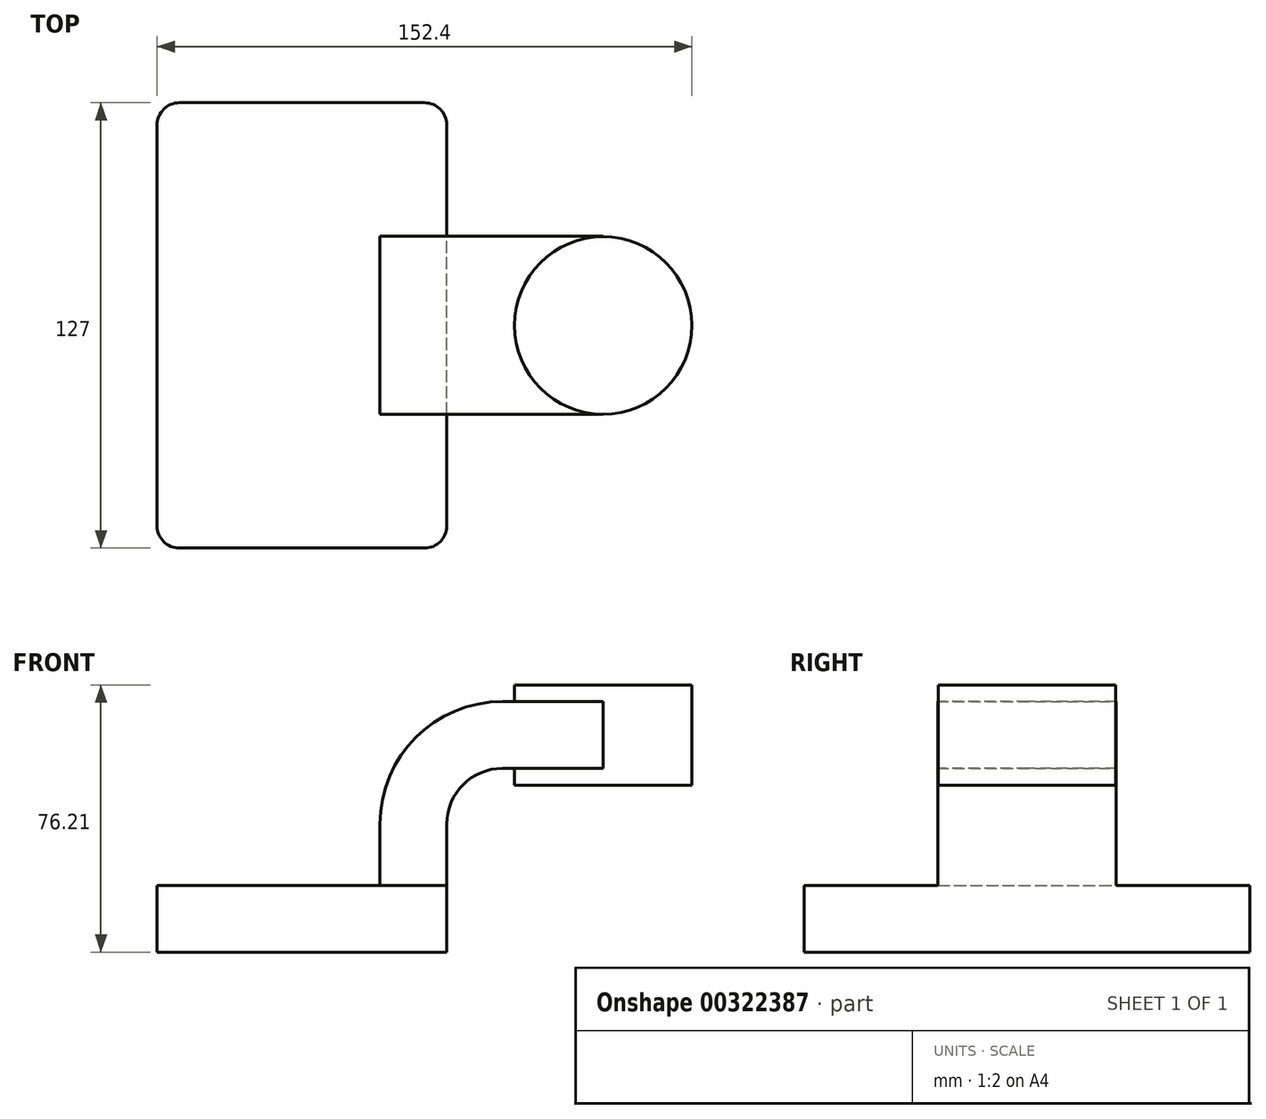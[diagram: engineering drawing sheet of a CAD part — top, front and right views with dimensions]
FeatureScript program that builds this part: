
annotation { "Feature Type Name" : "Feature", "Feature Type Description" : "" }
export const myFeature = defineFeature(function(context is Context, id is Id, definition is map)
    precondition{}
    {
        {
            var Q0;
            Q0=qCreatedBy(makeId("Front.planeOp"),FACE);
            var sketch = newSketch(context, id + "F0", { "sketchPlane" : qUnion([Q0])});
            skLineSegment(sketch, "E0.bottom", {"start": v(41.27, 9.53) * mm, "end": v(-41.28, 9.53) * mm});
            skLineSegment(sketch, "E0.top", {"start": v(41.28, -9.52) * mm, "end": v(-41.27, -9.52) * mm});
            skLineSegment(sketch, "E0.left", {"start": v(41.28, 9.53) * mm, "end": v(41.28, -9.52) * mm});
            skLineSegment(sketch, "E0.right", {"start": v(-41.28, 9.53) * mm, "end": v(-41.28, -9.52) * mm});
            skPoint(sketch, "E0.middle", {"position": v(0, 0) * mm});
            skLineSegment(sketch, "E1.bottom", {"start": v(111.12, 38.1) * mm, "end": v(60.32, 38.1) * mm});
            skLineSegment(sketch, "E1.top", {"start": v(111.12, 66.68) * mm, "end": v(60.32, 66.68) * mm});
            skLineSegment(sketch, "E1.left", {"start": v(111.12, 38.1) * mm, "end": v(111.12, 66.68) * mm});
            skLineSegment(sketch, "E1.right", {"start": v(60.32, 38.1) * mm, "end": v(60.32, 66.68) * mm});
            skPoint(sketch, "E1.middle", {"position": v(85.72, 52.39) * mm});
            skLineSegment(sketch, "E2", {"start": v(41.27, 9.53) * mm, "end": v(41.27, 27) * mm});
            skArc(sketch, "E3", {"start": v(41.27, 27) * mm, "mid": v(45.92, 38.23) * mm, "end": v(57.15, 42.88) * mm});
            skLineSegment(sketch, "E4", {"start": v(57.15, 42.88) * mm, "end": v(85.84, 42.88) * mm});
            skLineSegment(sketch, "E5.0", {"start": v(57.15, 61.93) * mm, "end": v(85.84, 61.93) * mm});
            skArc(sketch, "E5.1", {"start": v(22.22, 27) * mm, "mid": v(32.45, 51.7) * mm, "end": v(57.15, 61.93) * mm});
            skLineSegment(sketch, "E5.2", {"start": v(22.22, 9.53) * mm, "end": v(22.22, 27) * mm});
            skLineSegment(sketch, "E6", {"start": v(85.84, 38.1) * mm, "end": v(85.84, 66.68) * mm});
            skFitSpline(sketch, "E7", {"points": [v(-41.28, 9.53) * mm, v(57.15, 61.93) * mm], "startDerivative": vector(2.35, 85.99) * mm, "endDerivative": vector(119.19, -0.53) * mm});
            skSolve(sketch);
        }
        {
            var Q0;
            Q0=makeQuery(id+"F0.imprint","IMPRINT",FACE,{"disambiguationData":[TD([[makeQuery(id+"F0.imprint","IMPRINT",EDGE,{"derivedFrom":sQuery(id+"F0.wireOp",EDGE,"E0.top")}),-1.0]])]});
            extrude(context, id + "F1", {"entities" : qUnion([Q0]), "endBound" : BoundingType.SYMMETRIC, "depth" : 127 * mm});
        }
        {
            var Q0;
            {var subQ1=sQuery(id+"F0.wireOp",EDGE,"E2");Q0=makeQuery(id+"F0.imprint","IMPRINT",FACE,{"disambiguationData":[TD([[makeQuery(id+"F0.imprint","IMPRINT",EDGE,{"derivedFrom":subQ1}),1.0]])]});}
            var Q1;
            {var subQ0=sQuery(id+"F0.wireOp",EDGE,"E4");var subQ1=sQuery(id+"F0.wireOp",EDGE,"E1.right");var subQ2=makeQuery(id+"F0.imprint","INTERSECT",VERTEX,{"derivedFrom":[subQ1,subQ0]});Q1=makeQuery(id+"F0.imprint","IMPRINT",FACE,{"disambiguationData":[TD([[makeQuery(id+"F0.imprint","IMPRINT",EDGE,{"disambiguationData":[TD([[subQ2,-1.0]])],"derivedFrom":subQ1}),-1.0]])]});}
            extrude(context, id + "F2", {"entities" : qUnion([Q0, Q1]), "operationType" : NewBodyOperationType.ADD, "endBound" : BoundingType.SYMMETRIC, "depth" : 50.8 * mm});
        }
        {
            var Q0;
            Q0=makeQuery(id+"F0.imprint","IMPRINT",FACE,{"disambiguationData":[TD([[makeQuery(id+"F0.imprint","IMPRINT",EDGE,{"derivedFrom":sQuery(id+"F0.wireOp",EDGE,"E5.1")}),1.0]])]});
            extrude(context, id + "F3", {"entities" : qUnion([Q0]), "operationType" : NewBodyOperationType.ADD, "endBound" : BoundingType.SYMMETRIC, "depth" : 15.88 * mm});
        }
        {
            var Q0;
            {var subQ4=sQuery(id+"F0.wireOp",EDGE,"E1.left");Q0=makeQuery(id+"F0.imprint","IMPRINT",FACE,{"disambiguationData":[TD([[makeQuery(id+"F0.imprint","IMPRINT",EDGE,{"derivedFrom":subQ4}),1.0]])]});}
            var Q1;
            Q1=sQuery(id+"F0.wireOp",EDGE,"E6");
            revolve(context, id + "F4", {"operationType" : NewBodyOperationType.ADD, "entities" : qUnion([Q0]), "axis" : qUnion([Q1]), "revolveType" : RevolveType.FULL});
        }
        {
            var Q0;
            Q0=makeQuery(id+"F1.opExtrude","CAP_EDGE",EDGE,{"disambiguationData":[OSD([sQuery(id+"F0.wireOp",EDGE,"E0.left")])],"isStart":false});
            var Q1;
            Q1=makeQuery(id+"F1.opExtrude","CAP_EDGE",EDGE,{"disambiguationData":[OSD([sQuery(id+"F0.wireOp",EDGE,"E0.left")])],"isStart":true});
            var Q2;
            Q2=makeQuery(id+"F1.opExtrude","CAP_EDGE",EDGE,{"disambiguationData":[OSD([sQuery(id+"F0.wireOp",EDGE,"E0.right")])],"isStart":true});
            var Q3;
            Q3=makeQuery(id+"F1.opExtrude","CAP_EDGE",EDGE,{"disambiguationData":[OSD([sQuery(id+"F0.wireOp",EDGE,"E0.right")])],"isStart":false});
            fillet(context, id + "F5", {"entities" : qUnion([Q0, Q1, Q2, Q3]), "radius" : 6.35 * mm, "tangentPropagation" : true, "allowEdgeOverflow" : false});
        }
    });
